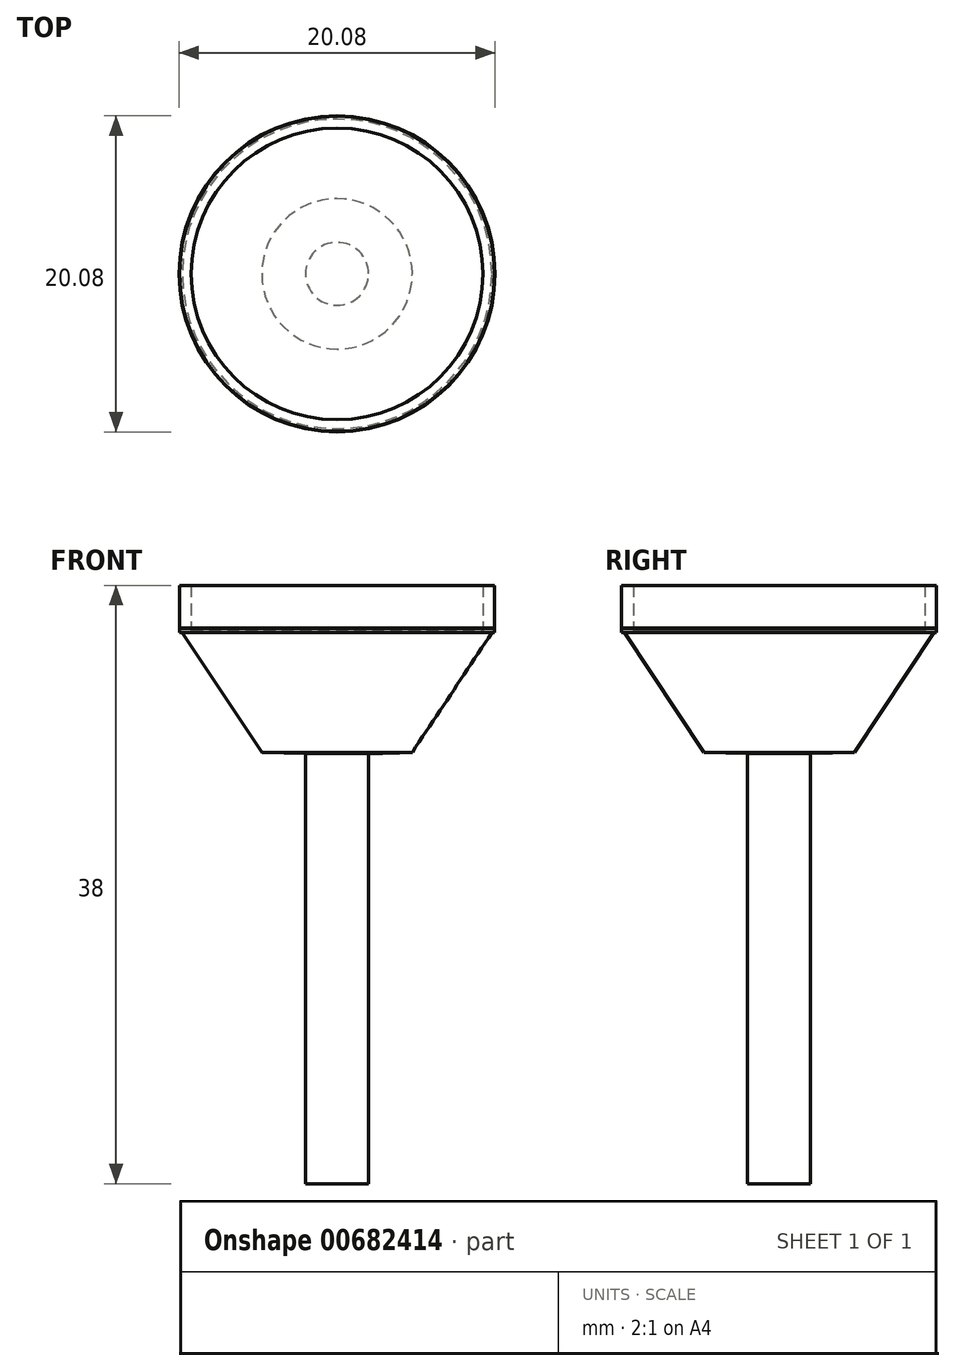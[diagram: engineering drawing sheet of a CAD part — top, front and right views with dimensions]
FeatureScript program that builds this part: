
annotation { "Feature Type Name" : "Feature", "Feature Type Description" : "" }
export const myFeature = defineFeature(function(context is Context, id is Id, definition is map)
    precondition{}
    {
        {
            var Q0;
            Q0=qCreatedBy(makeId("Top.planeOp"),FACE);
            var sketch = newSketch(context, id + "F0", { "sketchPlane" : qUnion([Q0])});
            skCircle(sketch, "E0", {"center": v(0, 0) * mm, "radius": 2 * mm});
            skSolve(sketch);
        }
        {
            var Q0;
            Q0=makeQuery(id+"F0.imprint","IMPRINT",FACE,{"disambiguationData":[TD([[makeQuery(id+"F0.imprint","IMPRINT",EDGE,{"derivedFrom":sQuery(id+"F0.wireOp",EDGE,"E0")}),1.0]])]});
            extrude(context, id + "F1", {"entities" : qUnion([Q0]), "depth" : 35 * mm, "offsetDistance" : 25 * mm});
        }
        {
            var Q0;
            Q0=makeQuery(id+"F1.opExtrude","CAP_FACE",FACE,{"disambiguationData":[OSD([sQuery(id+"F0.wireOp",EDGE,"E0")])],"isStart":false});
            var sketch = newSketch(context, id + "F2", { "sketchPlane" : qUnion([Q0])});
            skCircle(sketch, "E1", {"center": v(0, 0) * mm, "radius": 10 * mm});
            skSolve(sketch);
        }
        {
            var Q0;
            Q0 = qSketchRegion(id + "F2", true);
            extrude(context, id + "F3", {"entities" : qUnion([Q0]), "operationType" : NewBodyOperationType.ADD, "depth" : 3 * mm, "offsetDistance" : 25 * mm});
        }
        {
            var Q0;
            Q0=makeQuery(id+"F3.opExtrude","CAP_FACE",FACE,{"disambiguationData":[OSD([sQuery(id+"F2.wireOp",EDGE,"E1")])],"isStart":true});
            var sketch = newSketch(context, id + "F4", { "sketchPlane" : qUnion([Q0])});
            skCircle(sketch, "E2", {"center": v(0, 0) * mm, "radius": 4.64 * mm});
            skSolve(sketch);
        }
        {
            var Q0;
            Q0=qCreatedBy(makeId("Right.planeOp"),FACE);
            var sketch = newSketch(context, id + "F5", { "sketchPlane" : qUnion([Q0])});
            skLineSegment(sketch, "E3", {"start": v(0, 35.3) * mm, "end": v(-10.04, 35.3) * mm});
            skLineSegment(sketch, "E4", {"start": v(-10.04, 35.3) * mm, "end": v(-4.78, 27.4) * mm});
            skLineSegment(sketch, "E5", {"start": v(0, 31.3) * mm, "end": v(0, 25.34) * mm});
            skLineSegment(sketch, "E6", {"start": v(0, 35.3) * mm, "end": v(0, 27.25) * mm});
            skLineSegment(sketch, "E7", {"start": v(0, 27.25) * mm, "end": v(-4.78, 27.4) * mm});
            skSolve(sketch);
        }
        {
            var Q0;
            {var subQ0=sQuery(id+"F5.wireOp",EDGE,"E3");Q0=makeQuery(id+"F5.imprint","IMPRINT",FACE,{"disambiguationData":[TD([[makeQuery(id+"F5.imprint","IMPRINT",EDGE,{"derivedFrom":subQ0}),1.0]])]});}
            var Q1;
            Q1=sQuery(id+"F5.wireOp",EDGE,"E6");
            revolve(context, id + "F6", {"operationType" : NewBodyOperationType.ADD, "surfaceOperationType" : NewSurfaceOperationType.NEW, "entities" : qUnion([Q0]), "axis" : qUnion([Q1]), "revolveType" : RevolveType.FULL});
        }
        {
            var Q0;
            Q0=qCreatedBy(makeId("Front.planeOp"),FACE);
            var sketch = newSketch(context, id + "F7", { "sketchPlane" : qUnion([Q0])});
            skLineSegment(sketch, "E8", {"start": v(0, 38.9) * mm, "end": v(0, 35.14) * mm});
            skLineSegment(sketch, "E9", {"start": v(0, 35.14) * mm, "end": v(9.26, 35.14) * mm});
            skLineSegment(sketch, "E10", {"start": v(9.26, 35.14) * mm, "end": v(9.26, 40.56) * mm});
            skLineSegment(sketch, "E11", {"start": v(9.26, 40.56) * mm, "end": v(0, 38.9) * mm});
            skSolve(sketch);
        }
        {
            var Q0;
            Q0=makeQuery(id+"F7.imprint","IMPRINT",FACE,{"disambiguationData":[TD([[makeQuery(id+"F7.imprint","IMPRINT",EDGE,{"derivedFrom":sQuery(id+"F7.wireOp",EDGE,"E8")}),1.0]])]});
            var Q1;
            Q1=sQuery(id+"F7.wireOp",EDGE,"E8");
            revolve(context, id + "F8", {"operationType" : NewBodyOperationType.REMOVE, "surfaceOperationType" : NewSurfaceOperationType.NEW, "entities" : qUnion([Q0]), "axis" : qUnion([Q1]), "revolveType" : RevolveType.FULL, "oppositeDirection" : true});
        }
    });
